# Revit family: Gira_543000
name_source: partatom
category: Elektroinstallationen
revit_build: Autodesk Revit 2017 (Build: 20160225_1515(x64)
units: mm (PartAtom-declared; Revit-internal decimal feet)

## family parameters
Basisbauteil = Fläche
Beim Laden mit Abzugskörper schneiden = Nein
Bemaßung runder Anschluss = Durchmesser verwenden
Beschriftungsausrichtung beibehalten = Nein
Gemeinsam genutzt = Nein
Raumberechnungspunkt = Nein
Teiletyp = Normal

## types (1)
- Funk Dimmaktor 1f REG Gira eNet
    Andere Bussysteme = eNet
    Anzahl der Ausgänge = 1
    Anzahl der Eingänge = 0
    Anzahl der binären Eingänge = 0
    App-Steuerung über Bluetooth = Nein
    Ausführung Text = Dimmaktor
    Ausgangsleistung [Voltampere] = [500:500]
    BIM = https://media.stage.bim.site X1 REG KNX.rfa
    BIMSITE_PRODUCT_ID = a9636d8d94fcf1a9dfd08dc613c52d40db9e02c7
    Beschreibung = eNet Funk Dimmaktor 1fach 20 - 500 W VA REG Merkmale: Mit eNet Server einstellbar::  Vollverschlüsselte Funkübertragung (AES-CCM) ab eNet Server Software Version 2.0.  Bediensperren.  Update der Gerätesoftware.  Der eNet Funk Dimmaktor empfängt über eine Datenleitung vom eNet Funk Empfangsmodul oder eNet Server Telegramme zum Schalten und Dimmen verschiedener elektrischer Lasten.  Schalten und Dimmen von Glühlampen, HV-Halogenlampen, elektronischen Trafos für Halogen- oder LED-Lampen, dimmbaren induktiven Trafos für Halogen- oder LED-Lampen, HV-LED- oder Kompaktleuchtstofflampen.  Lampenschonendes Einschalten.  Einschalt- und Minimalhelligkeit speicherbar.  Szenenbetrieb.  Statusanzeige mit LED.  Statusrückmeldung an eNet Funksensoren.  Kurzschluss- und Übertemperaturschutz.  Automatische oder manuelle Einstellung des Dimmverfahrens. Mit eNet Server einstellbar::  Maximale Helligkeit.  Dimmverfahren.  Dimmgeschwindigkeit.  Nachlaufzeit.  Ein- bzw. Ausschaltverzögerung.  Auf- bzw. Abdimmrampe.  Abschaltvorwarnung.  Dauer-Ein, Dauer-Aus.  Hotelfunktion.  Lichtregelung.  Hinweise :  Zum Betrieb dieses Reiheneinbaugeräts wird ein eNet Funk Empfangsmodul oder ein eNet Server benötigt.
    Breite in Teilungseinheiten = 2
    Bussystem Funkbus = Ja
    Bussystem KNX = Nein
    Bussystem KNX-Funk = Nein
    Bussystem LON = Nein
    Bussystem Powernet = Nein
    Datenblatt = https://media.stage.bim.site
    Datenblatt 1 = https://media.stage.bim.site
    Dimmung Phasenabschnitt = Nein
    Dimmung Phasenanschnitt = Nein
    Funk bidirektional = Nein
    Funktion Schalten = Nein
    GTIN = 4010337774259
    Geeignet für C-Last = Nein
    HAN = 543000
    Halogenfrei = Nein
    HeinzeBIM = https://www.heinze.de
    Hersteller = Gira
    Kosten = 0 $
    Lastart = universal
    Leistungszusatz verwendbar = Nein
    Lichtwertspeicher = Nein
    Max. Anzahl der Jalousieausgänge = 0
    Max. Anzahl der Schaltausgänge = 0
    Max. Schaltleistung [Voltampere] = 0
    Mit Beschriftungsfeld = Nein
    Mit Busankopplung = Nein
    Mit LED-Anzeige = Ja
    Modulare Erweiterungsmöglichkeit = Nein
    Montageart = REG
    Nebenstelleneingang = Nein
    Parallel-Betrieb möglich = Nein
    Produktseite = https://media.stage.bim.site
    Schutzart (IP) = IP20
    Seriendimmer = Nein
    Transparent = Nein
    Typname = Funk Dimmaktor 1f REG Gira eNet
    URL = https://www.gira.de
    Verschiedene Phasen anschließbar = Nein
    Verwendbar mit Bewegungsmelder = Nein
    Verwendbar mit Funktaste = Nein
    Verwendbar mit IR-Taste = Nein
    Verwendbar mit Präsenzmelder = Nein
    Verwendbar mit Taste = Nein
    Verwendbar mit Zeitschalter/Timer = Nein
    Vor Ort-/Handbedienung = Nein
    Vorgabe-Ansicht = 1219 mm

## geometry (parser evidence)
native form markers: Sweep x2
no freeform markers — native parametric forms only
